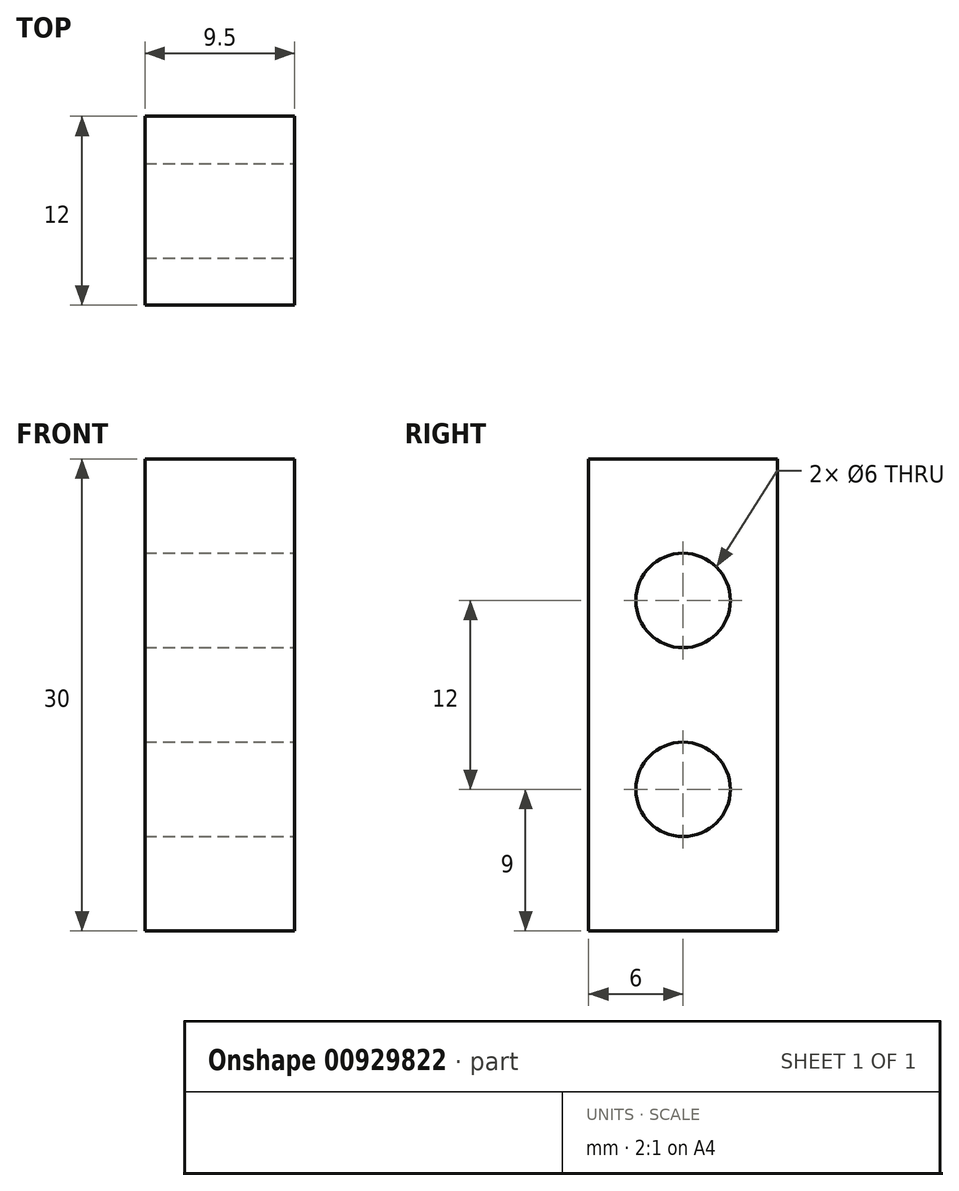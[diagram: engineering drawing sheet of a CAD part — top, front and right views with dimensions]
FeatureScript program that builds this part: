
annotation { "Feature Type Name" : "Feature", "Feature Type Description" : "" }
export const myFeature = defineFeature(function(context is Context, id is Id, definition is map)
    precondition{}
    {
        {
            var Q0;
            Q0=qCreatedBy(makeId("Right.planeOp"),FACE);
            var sketch = newSketch(context, id + "F0", { "sketchPlane" : qUnion([Q0])});
            skLineSegment(sketch, "E0", {"start": v(-12, 0) * mm, "end": v(-12, 30) * mm});
            skLineSegment(sketch, "E1", {"start": v(-12, 30) * mm, "end": v(0, 30) * mm});
            skLineSegment(sketch, "E2", {"start": v(-12, 0) * mm, "end": v(0, 0) * mm});
            skLineSegment(sketch, "E3", {"start": v(0, 0) * mm, "end": v(0, 30) * mm});
            skSolve(sketch);
        }
        {
            var Q0;
            Q0=makeQuery(id+"F0.imprint","IMPRINT",FACE,{"disambiguationData":[TD([[makeQuery(id+"F0.imprint","IMPRINT",EDGE,{"derivedFrom":sQuery(id+"F0.wireOp",EDGE,"E0")}),-1.0]])]});
            extrude(context, id + "F1", {"entities" : qUnion([Q0]), "depth" : 9.5 * mm, "offsetDistance" : 25 * mm});
        }
        {
            var Q0;
            Q0=makeQuery(id+"F1.opExtrude","CAP_FACE",FACE,{"disambiguationData":[OSD([sQuery(id+"F0.wireOp",EDGE,"E0"),sQuery(id+"F0.wireOp",EDGE,"E1"),sQuery(id+"F0.wireOp",EDGE,"E2"),sQuery(id+"F0.wireOp",EDGE,"E3")])],"isStart":false});
            var sketch = newSketch(context, id + "F2", { "sketchPlane" : qUnion([Q0])});
            skLineSegment(sketch, "E4", {"start": v(-6, 0) * mm, "end": v(-6, 9) * mm});
            skLineSegment(sketch, "E5", {"start": v(-6, 9) * mm, "end": v(-6, 21) * mm});
            skSolve(sketch);
        }
        {
            var Q0;
            Q0=sQuery(id+"F2.wireOp",VERTEX,"E4.end");
            var Q1;
            Q1=makeQuery(id+"F1.opExtrude","SWEPT_BODY",BODY,{"disambiguationData":[OSD([sQuery(id+"F0.wireOp",EDGE,"E0"),sQuery(id+"F0.wireOp",EDGE,"E1"),sQuery(id+"F0.wireOp",EDGE,"E2"),sQuery(id+"F0.wireOp",EDGE,"E3")])]});
            hole(context, id + "F3", {"style" : HoleStyle.SIMPLE, "endStyle" : HoleEndStyle.THROUGH, "holeDiameter" : 6 * mm, "majorDiameter" : 5 * mm, "isTappedThrough" : true, "tappedDepth" : 12 * mm, "tapClearance" : 3, "locations" : qUnion([Q0]), "scope" : qUnion([Q1])});
        }
        {
            var Q0;
            Q0=sQuery(id+"F2.wireOp",VERTEX,"E5.end");
            var Q1;
            Q1=makeQuery(id+"F1.opExtrude","SWEPT_BODY",BODY,{"disambiguationData":[OSD([sQuery(id+"F0.wireOp",EDGE,"E0"),sQuery(id+"F0.wireOp",EDGE,"E1"),sQuery(id+"F0.wireOp",EDGE,"E2"),sQuery(id+"F0.wireOp",EDGE,"E3")])]});
            hole(context, id + "F4", {"style" : HoleStyle.SIMPLE, "endStyle" : HoleEndStyle.THROUGH, "holeDiameter" : 6 * mm, "majorDiameter" : 5 * mm, "isTappedThrough" : true, "tappedDepth" : 12 * mm, "tapClearance" : 3, "locations" : qUnion([Q0]), "scope" : qUnion([Q1])});
        }
    });
